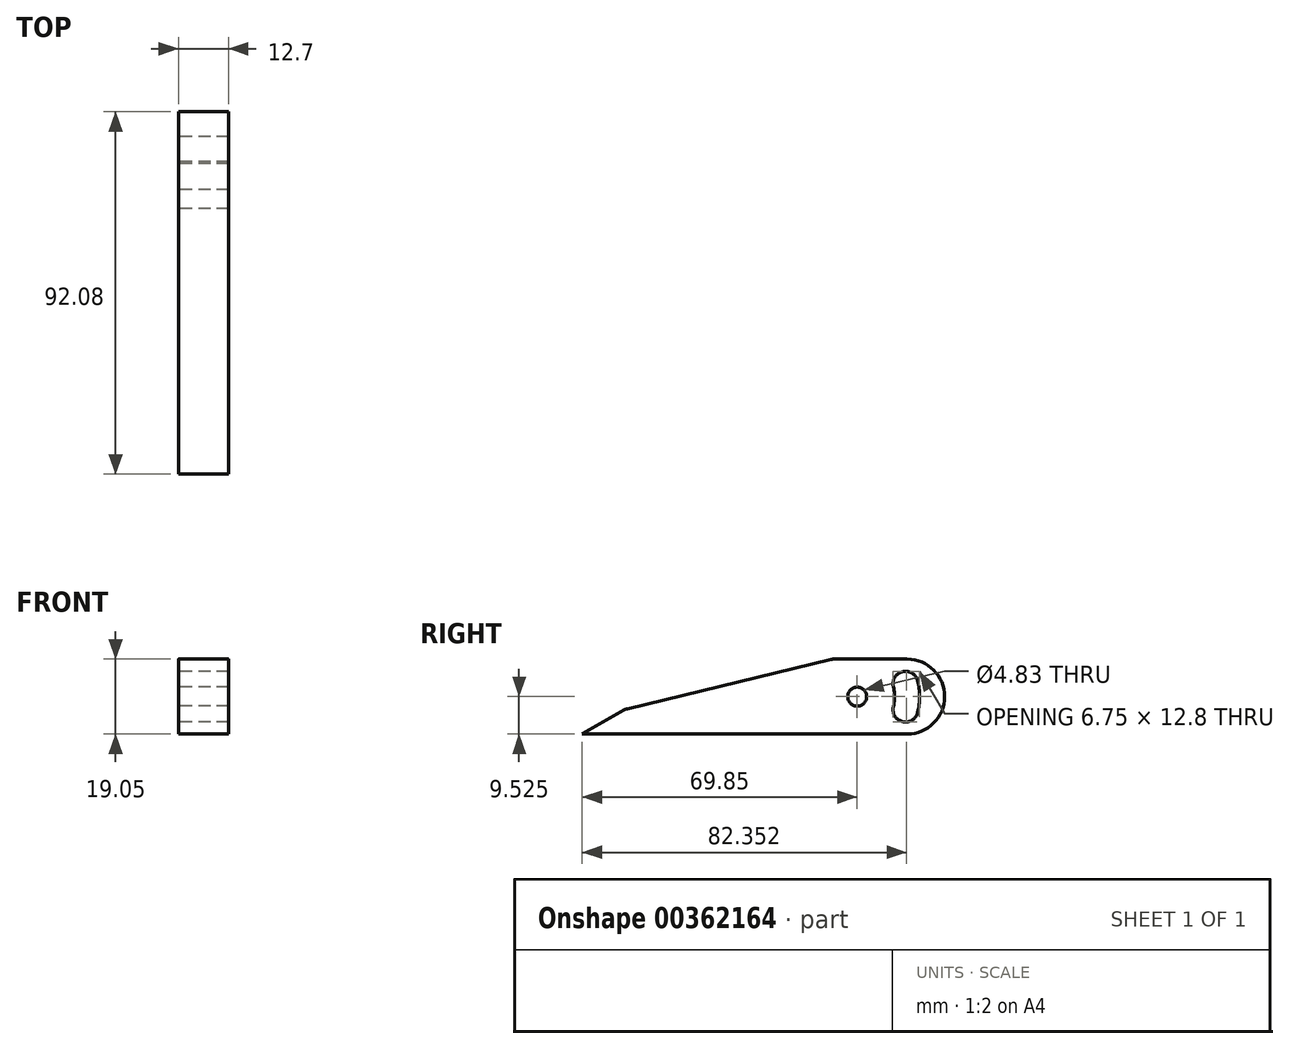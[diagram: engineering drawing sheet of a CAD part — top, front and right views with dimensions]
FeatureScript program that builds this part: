
annotation { "Feature Type Name" : "Feature", "Feature Type Description" : "" }
export const myFeature = defineFeature(function(context is Context, id is Id, definition is map)
    precondition{}
    {
        {
            var Q0;
            Q0=qCreatedBy(makeId("Right.planeOp"),FACE);
            var sketch = newSketch(context, id + "F0", { "sketchPlane" : qUnion([Q0])});
            skLineSegment(sketch, "E0", {"start": v(0, 0) * mm, "end": v(82.55, 0) * mm});
            skLineSegment(sketch, "E1", {"start": v(0, 0) * mm, "end": v(11, 6.35) * mm});
            skArc(sketch, "E2", {"start": v(82.55, 0) * mm, "mid": v(92.08, 9.53) * mm, "end": v(82.55, 19.05) * mm});
            skLineSegment(sketch, "E3", {"start": v(82.55, 9.53) * mm, "end": v(69.85, 9.53) * mm, "construction": true});
            skLineSegment(sketch, "E4", {"start": v(82.55, 19.05) * mm, "end": v(63.5, 19.05) * mm});
            skLineSegment(sketch, "E5", {"start": v(63.5, 19.05) * mm, "end": v(11, 6.35) * mm});
            skLineSegment(sketch, "E6", {"start": v(82.55, 9.53) * mm, "end": v(82.55, 19.05) * mm, "construction": true});
            skLineSegment(sketch, "E7", {"start": v(69.85, 9.53) * mm, "end": v(69.85, 19.05) * mm, "construction": true});
            skArc(sketch, "E8", {"start": v(85.2, 13.6) * mm, "mid": v(85.73, 9.52) * mm, "end": v(85.2, 5.46) * mm});
            skArc(sketch, "E9", {"start": v(79.06, 11.97) * mm, "mid": v(79.38, 9.52) * mm, "end": v(79.06, 7.08) * mm});
            skLineSegment(sketch, "E10", {"start": v(69.85, 9.53) * mm, "end": v(69.85, 9.53) * mm});
            skLineSegment(sketch, "E11", {"start": v(79.06, 7.08) * mm, "end": v(85.2, 5.46) * mm, "construction": true});
            skArc(sketch, "E12", {"start": v(79.06, 7.08) * mm, "mid": v(81.31, 3.2) * mm, "end": v(85.2, 5.46) * mm});
            skArc(sketch, "E13", {"start": v(79.06, 11.97) * mm, "mid": v(81.31, 15.85) * mm, "end": v(85.2, 13.6) * mm});
            skLineSegment(sketch, "E14", {"start": v(79.38, 9.53) * mm, "end": v(85.72, 9.53) * mm, "construction": true});
            skLineSegment(sketch, "E15", {"start": v(82.13, 6.27) * mm, "end": v(82.55, 9.53) * mm, "construction": true});
            skLineSegment(sketch, "E16", {"start": v(82.13, 12.78) * mm, "end": v(82.55, 9.52) * mm, "construction": true});
            skLineSegment(sketch, "E17", {"start": v(69.85, 9.53) * mm, "end": v(82.47, 8.07) * mm, "construction": true});
            skPoint(sketch, "E18", {"position": v(82.47, 8.07) * mm});
            skLineSegment(sketch, "E19", {"start": v(69.85, 9.53) * mm, "end": v(2, 17.35) * mm, "construction": true});
            skLineSegment(sketch, "E20", {"start": v(2, 17.35) * mm, "end": v(0, 0) * mm, "construction": true});
            skSolve(sketch);
        }
        {
            var Q0;
            Q0=makeQuery(id+"F0.imprint","IMPRINT",FACE,{"disambiguationData":[TD([[makeQuery(id+"F0.imprint","IMPRINT",EDGE,{"derivedFrom":sQuery(id+"F0.wireOp",EDGE,"E0")}),1.0]])]});
            extrude(context, id + "F1", {"entities" : qUnion([Q0]), "depth" : 12.7 * mm, "offsetDistance" : 25.4 * mm});
        }
        {
            var Q0;
            Q0=sQuery(id+"F0.wireOp",VERTEX,"E7.start");
            var Q1;
            Q1=sQuery(id+"F0.wireOp",VERTEX,"E18");
            var Q2;
            Q2=makeQuery(id+"F1.opExtrude","SWEPT_BODY",BODY,{"disambiguationData":[OSD([sQuery(id+"F0.wireOp",EDGE,"E0"),sQuery(id+"F0.wireOp",EDGE,"E1"),sQuery(id+"F0.wireOp",EDGE,"E2"),sQuery(id+"F0.wireOp",EDGE,"E4"),sQuery(id+"F0.wireOp",EDGE,"E5")])]});
            hole(context, id + "F2", {"style" : HoleStyle.SIMPLE, "endStyle" : HoleEndStyle.THROUGH, "oppositeDirection" : true, "holeDiameter" : 4.83 * mm, "isTappedThrough" : true, "tappedDepth" : 12.7 * mm, "tapClearance" : 3, "startFromSketch" : true, "locations" : qUnion([Q0, Q1]), "scope" : qUnion([Q2])});
        }
        {
            var Q0;
            Q0=makeQuery(id+"F1.opExtrude","SWEPT_EDGE",EDGE,{"disambiguationData":[OSD([sQuery(id+"F0.wireOp",EDGE,"E4"),sQuery(id+"F0.wireOp",EDGE,"E5")])]});
            var Q1;
            Q1=makeQuery(id+"F1.opExtrude","SWEPT_EDGE",EDGE,{"disambiguationData":[OSD([sQuery(id+"F0.wireOp",EDGE,"E1"),sQuery(id+"F0.wireOp",EDGE,"E5")])]});
            fillet(context, id + "F3", {"entities" : qUnion([Q0, Q1]), "radius" : 3.17 * mm, "tangentPropagation" : true, "allowEdgeOverflow" : false});
        }
    });
